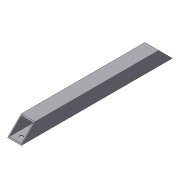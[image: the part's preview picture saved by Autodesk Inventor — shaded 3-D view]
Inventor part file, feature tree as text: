
AUTODESK INVENTOR PART (.ipt)
format: ipt  version: 2012 (Build 160160000, 160)  size: 101,888 bytes
history: native  units: in
note: dims shown in document units (in); Inventor stores cm internally (conversion verified against a paired STEP export)
features: extrude x4, sketch x4, shell x1
ambient origin geometry x8: Origin, YZ Plane, XZ Plane, XY Plane, X Axis, Y Axis, Z Axis, Center Point
bodies: Solid1 (feature_tree)
feature tree (9):
  extrude  "Extrusion1"  Depth=1.0in
  shell  "Shell1"  Thickness=11.0in
  extrude  "Extrusion2"  Depth=1.0in
  extrude  "Extrusion3"  Depth=11.0in TaperAngle=0.0deg
  extrude  "Extrusion4"  Depth=0.5in
  sketch  "Sketch1"  dims[d0=1.0in d1=1.0in d2=11.0in d3=0.0in]
  sketch  "Sketch2"  dims[d4=0.0625in d5=1.0in]
  sketch  "Sketch3"  dims[d6=1.0in d7=11.0in d8=0.0in]
  sketch  "Sketch4"  dims[d9=0.25in d10=0.5in d11=0.5in d12=0.5in d13=0.5in d14=11.0in d15=0.0in d16=11.0in d17=0.0in]
